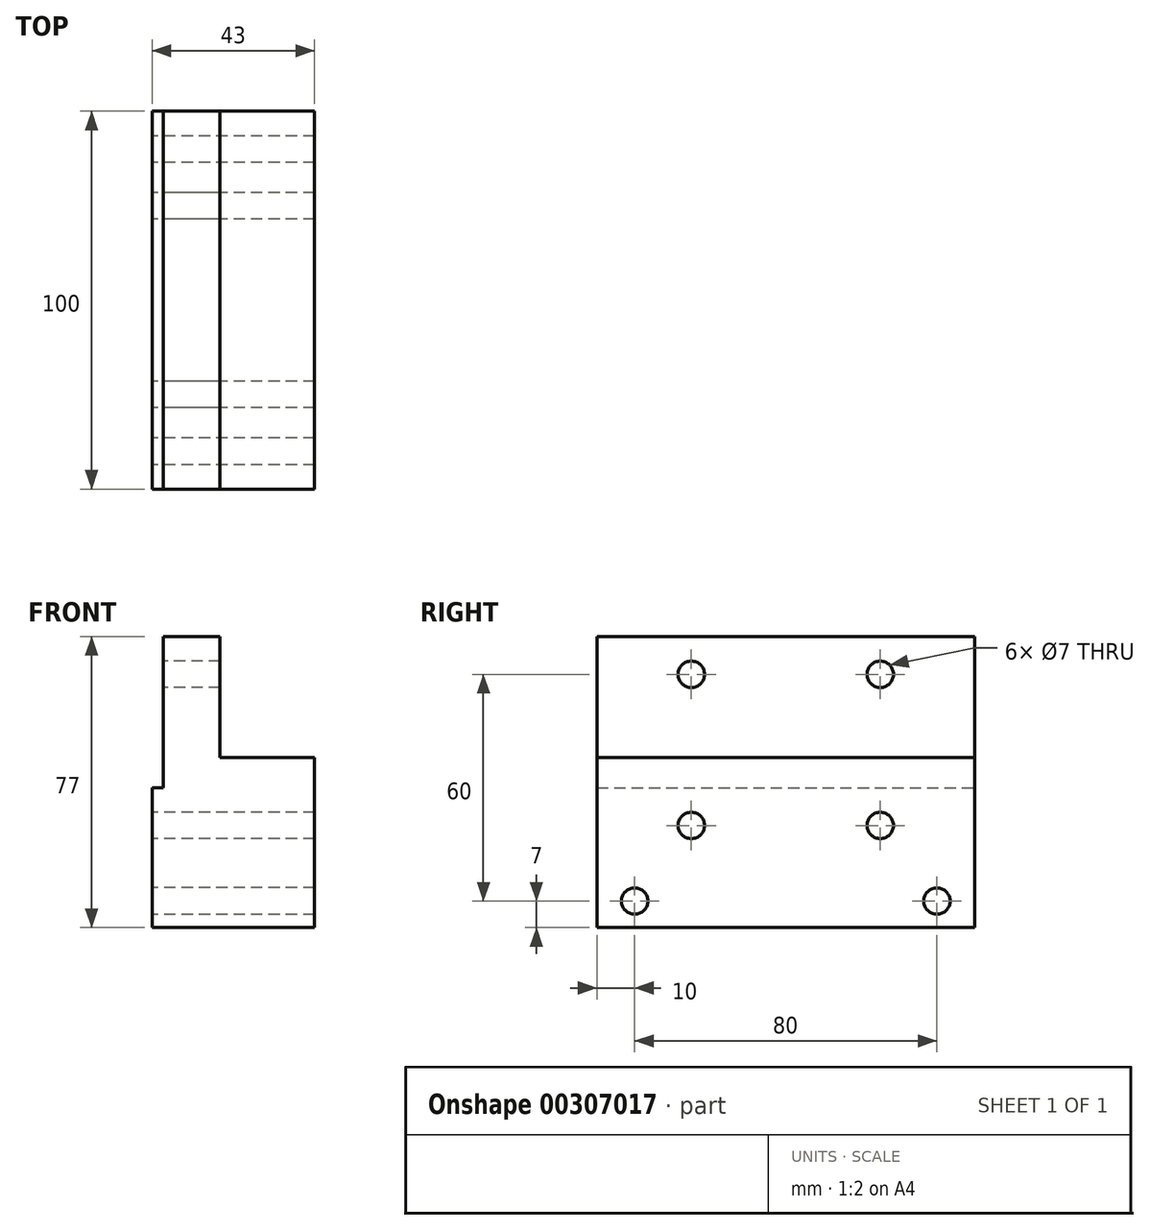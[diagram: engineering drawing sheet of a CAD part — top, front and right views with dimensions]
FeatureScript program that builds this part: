
annotation { "Feature Type Name" : "Feature", "Feature Type Description" : "" }
export const myFeature = defineFeature(function(context is Context, id is Id, definition is map)
    precondition{}
    {
        {
            var Q0;
            Q0=qCreatedBy(makeId("Front.planeOp"),FACE);
            var sketch = newSketch(context, id + "F0", { "sketchPlane" : qUnion([Q0])});
            skLineSegment(sketch, "E0.top", {"start": v(5.27, -37) * mm, "end": v(48.27, -37) * mm});
            skLineSegment(sketch, "E0.left", {"start": v(5.27, 0) * mm, "end": v(5.27, -37) * mm});
            skLineSegment(sketch, "E0.right", {"start": v(48.27, 8) * mm, "end": v(48.27, -37) * mm});
            skLineSegment(sketch, "E1", {"start": v(5.27, 0) * mm, "end": v(8.27, 0) * mm});
            skLineSegment(sketch, "E2", {"start": v(8.27, 0) * mm, "end": v(8.27, 40) * mm});
            skLineSegment(sketch, "E3", {"start": v(48.27, 8) * mm, "end": v(23.27, 8) * mm});
            skLineSegment(sketch, "E4", {"start": v(23.27, 8) * mm, "end": v(23.27, 40) * mm});
            skLineSegment(sketch, "E5", {"start": v(23.27, 40) * mm, "end": v(8.27, 40) * mm});
            skSolve(sketch);
        }
        {
            var Q0;
            Q0 = qSketchRegion(id + "F0", true);
            extrude(context, id + "F1", {"entities" : qUnion([Q0]), "depth" : 100 * mm});
        }
        {
            var Q0;
            Q0=makeQuery(id+"F1.opExtrude","SWEPT_FACE",FACE,{"disambiguationData":[OSD([sQuery(id+"F0.wireOp",EDGE,"E2")])]});
            var sketch = newSketch(context, id + "F2", { "sketchPlane" : qUnion([Q0])});
            skCircle(sketch, "E6", {"center": v(25, 30) * mm, "radius": 3.5 * mm});
            skCircle(sketch, "E7", {"center": v(75, 30) * mm, "radius": 3.5 * mm});
            skCircle(sketch, "E8", {"center": v(25, -10) * mm, "radius": 3.5 * mm});
            skCircle(sketch, "E9", {"center": v(75, -10) * mm, "radius": 3.5 * mm});
            skCircle(sketch, "E10", {"center": v(90, -30) * mm, "radius": 3.5 * mm});
            skCircle(sketch, "E11", {"center": v(10, -30) * mm, "radius": 3.5 * mm});
            skSolve(sketch);
        }
        {
            var Q0;
            Q0 = qSketchRegion(id + "F2", true);
            extrude(context, id + "F3", {"entities" : qUnion([Q0]), "operationType" : NewBodyOperationType.REMOVE, "oppositeDirection" : true, "depth" : 100 * mm, "symmetric" : true});
        }
    });
